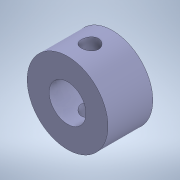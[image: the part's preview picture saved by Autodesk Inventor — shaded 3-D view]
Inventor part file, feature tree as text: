
AUTODESK INVENTOR PART (.ipt)
format: ipt  version: 2021 (Build 250183000, 183)  size: 118,784 bytes
history: native  units: mm
features: extrude x2, sketch x2
ambient origin geometry x8: Origin, YZ Plane, XZ Plane, XY Plane, X Axis, Y Axis, Z Axis, Center Point
bodies: Solid1 (feature_tree)
feature tree (4):
  extrude  "Extrusion1"  Depth=18.0mm
  extrude  "Extrusion2"  Depth=10.0mm
  sketch  "Sketch1"  dims[d0=8.2mm d1=18.0mm]
  sketch  "Sketch2"  dims[d2=10.0mm d3=0.0mm d4=3.8mm d5=11.0mm d6=11.0mm d7=0.0mm d8=0.0mm]
